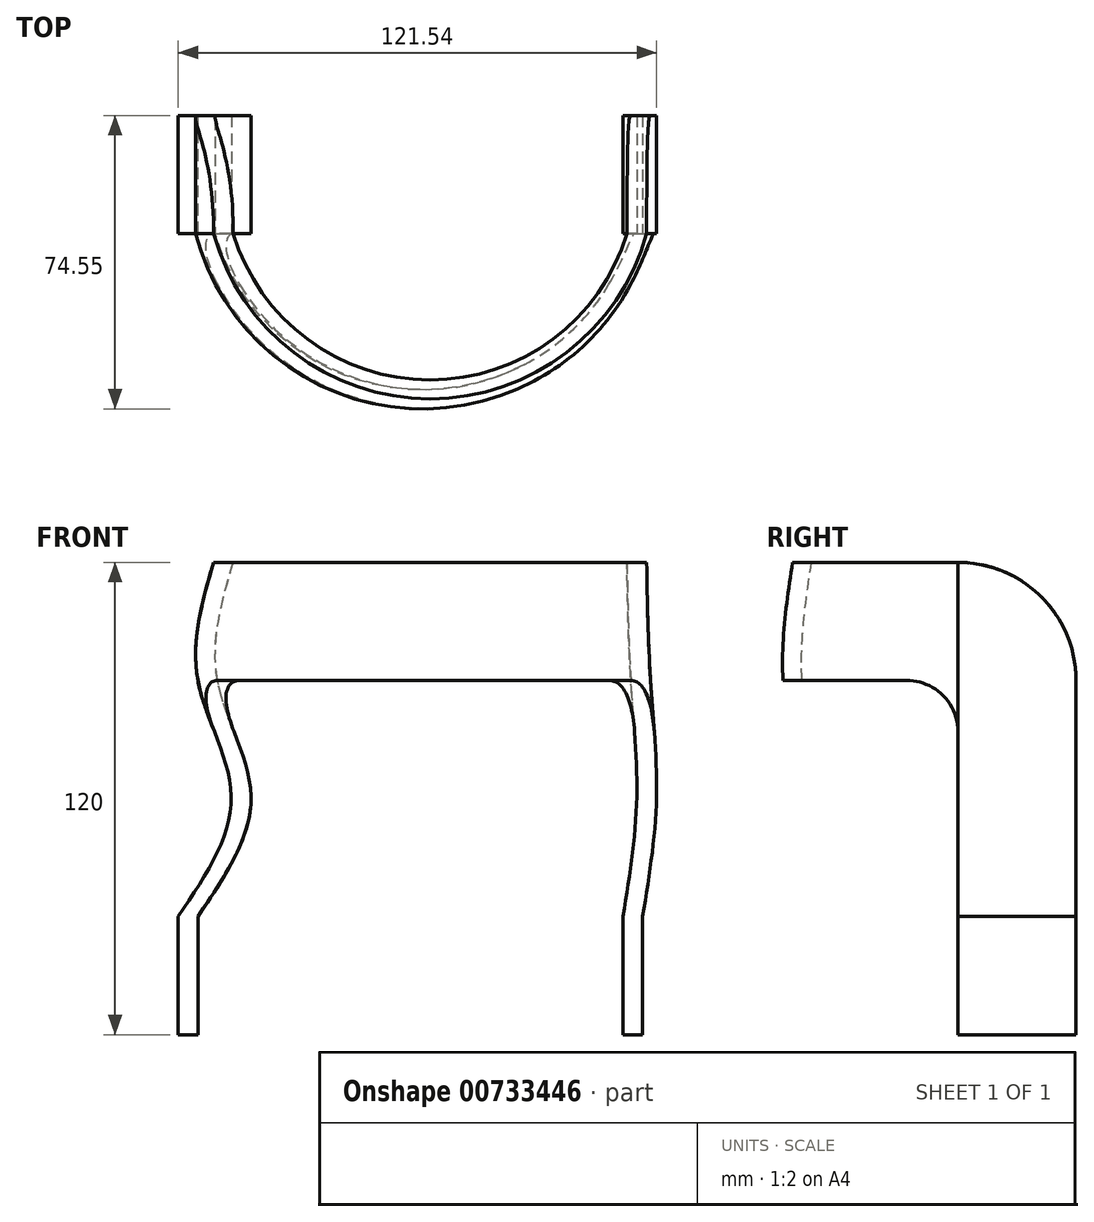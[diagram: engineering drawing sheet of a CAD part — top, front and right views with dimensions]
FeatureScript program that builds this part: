
annotation { "Feature Type Name" : "Feature", "Feature Type Description" : "" }
export const myFeature = defineFeature(function(context is Context, id is Id, definition is map)
    precondition{}
    {
        {
            var Q0;
            Q0=qCreatedBy(makeId("Top.planeOp"),FACE);
            cPlane(context, id + "F0", {"entities" : qUnion([Q0]), "cplaneType" : CPlaneType.OFFSET, "offset" : 30 * mm, "width" : 150 * mm, "height" : 150 * mm});
        }
        {
            var Q0;
            Q0=qCreatedBy(id+"F0.planeOp",FACE);
            var sketch = newSketch(context, id + "F1", { "sketchPlane" : qUnion([Q0])});
            skLineSegment(sketch, "E0", {"start": v(-54, 0) * mm, "end": v(-54, 15) * mm});
            skLineSegment(sketch, "E1", {"start": v(-54, 15) * mm, "end": v(-59, 15) * mm});
            skLineSegment(sketch, "E2", {"start": v(-59, 15) * mm, "end": v(-59, -15) * mm});
            skLineSegment(sketch, "E3", {"start": v(-54, -15) * mm, "end": v(-54, 0) * mm});
            skLineSegment(sketch, "E4", {"start": v(54, 0) * mm, "end": v(54, 15) * mm});
            skLineSegment(sketch, "E5", {"start": v(54, 15) * mm, "end": v(59, 15) * mm});
            skLineSegment(sketch, "E6", {"start": v(59, 15) * mm, "end": v(59, -15) * mm});
            skLineSegment(sketch, "E7", {"start": v(54, -15) * mm, "end": v(54, 0) * mm});
            skArc(sketch, "E8", {"start": v(-54, -15) * mm, "mid": v(0, -56.04) * mm, "end": v(54, -15) * mm});
            skArc(sketch, "E9", {"start": v(59, -15) * mm, "mid": v(0, -60.88) * mm, "end": v(-59, -15) * mm});
            skPoint(sketch, "E10", {"position": v(0, -56.04) * mm});
            skPoint(sketch, "E11", {"position": v(0, -60.88) * mm});
            skSolve(sketch);
        }
        {
            var Q0;
            Q0=qCreatedBy(makeId("Top.planeOp"),FACE);
            var sketch = newSketch(context, id + "F2", { "sketchPlane" : qUnion([Q0])});
            skLineSegment(sketch, "E12", {"start": v(-54, 0) * mm, "end": v(-54, 15) * mm});
            skLineSegment(sketch, "E13", {"start": v(-54, 15) * mm, "end": v(-59, 15) * mm});
            skLineSegment(sketch, "E14", {"start": v(-59, 15) * mm, "end": v(-59, -15) * mm});
            skLineSegment(sketch, "E15", {"start": v(-54, -15) * mm, "end": v(-54, 0) * mm});
            skLineSegment(sketch, "E16", {"start": v(54, 0) * mm, "end": v(54, 15) * mm});
            skLineSegment(sketch, "E17", {"start": v(54, 15) * mm, "end": v(59, 15) * mm});
            skLineSegment(sketch, "E18", {"start": v(59, 15) * mm, "end": v(59, -15) * mm});
            skLineSegment(sketch, "E19", {"start": v(54, -15) * mm, "end": v(54, 0) * mm});
            skArc(sketch, "E20", {"start": v(-54, -15) * mm, "mid": v(0, -56.04) * mm, "end": v(54, -15) * mm});
            skArc(sketch, "E21", {"start": v(59, -15) * mm, "mid": v(0, -60.88) * mm, "end": v(-59, -15) * mm});
            skPoint(sketch, "E22", {"position": v(0, -56.04) * mm});
            skPoint(sketch, "E23", {"position": v(0, -60.88) * mm});
            skSolve(sketch);
        }
        {
            var Q0;
            Q0=qCreatedBy(makeId("Top.planeOp"),FACE);
            cPlane(context, id + "F3", {"entities" : qUnion([Q0]), "cplaneType" : CPlaneType.OFFSET, "offset" : 60 * mm, "width" : 150 * mm, "height" : 150 * mm});
        }
        {
            var Q0;
            Q0=qCreatedBy(id+"F3.planeOp",FACE);
            var sketch = newSketch(context, id + "F4", { "sketchPlane" : qUnion([Q0])});
            skPoint(sketch, "E24", {"position": v(8.5, 0) * mm});
            skPoint(sketch, "E25", {"position": v(-40.5, 0) * mm});
            skPoint(sketch, "E26", {"position": v(57.5, 0) * mm});
            skLineSegment(sketch, "E27", {"start": v(-40.5, 0) * mm, "end": v(-40.5, -15) * mm});
            skLineSegment(sketch, "E28", {"start": v(-45.5, -15) * mm, "end": v(-45.5, 15) * mm});
            skLineSegment(sketch, "E29", {"start": v(-45.5, 15) * mm, "end": v(-40.5, 15) * mm});
            skLineSegment(sketch, "E30", {"start": v(-40.5, 15) * mm, "end": v(-40.5, 0) * mm});
            skLineSegment(sketch, "E31", {"start": v(57.5, 0) * mm, "end": v(57.5, 15) * mm});
            skLineSegment(sketch, "E32", {"start": v(57.5, 15) * mm, "end": v(62.5, 15) * mm});
            skLineSegment(sketch, "E33", {"start": v(62.5, 15) * mm, "end": v(62.5, -15) * mm});
            skLineSegment(sketch, "E34", {"start": v(57.5, -15) * mm, "end": v(57.5, 0) * mm});
            skArc(sketch, "E35", {"start": v(-40.5, -15) * mm, "mid": v(8.5, -51.24) * mm, "end": v(57.5, -15) * mm});
            skArc(sketch, "E36", {"start": v(-45.5, -15) * mm, "mid": v(8.5, -56.04) * mm, "end": v(62.5, -15) * mm});
            skSolve(sketch);
        }
        {
            var Q0;
            Q0=qCreatedBy(makeId("Top.planeOp"),FACE);
            cPlane(context, id + "F5", {"entities" : qUnion([Q0]), "cplaneType" : CPlaneType.OFFSET, "offset" : 90 * mm, "width" : 150 * mm, "height" : 150 * mm});
        }
        {
            var Q0;
            Q0=qCreatedBy(id+"F5.planeOp",FACE);
            var sketch = newSketch(context, id + "F6", { "sketchPlane" : qUnion([Q0])});
            skPoint(sketch, "E37", {"position": v(3.5, 0) * mm});
            skPoint(sketch, "E38", {"position": v(-49, 0) * mm});
            skPoint(sketch, "E39", {"position": v(56, 0) * mm});
            skLineSegment(sketch, "E40", {"start": v(-49, 0) * mm, "end": v(-49, 15) * mm});
            skLineSegment(sketch, "E41", {"start": v(-49, 15) * mm, "end": v(-54, 15) * mm});
            skLineSegment(sketch, "E42", {"start": v(-54, 15) * mm, "end": v(-54, -15) * mm});
            skLineSegment(sketch, "E43", {"start": v(-49, -15) * mm, "end": v(-49, 0) * mm});
            skLineSegment(sketch, "E44", {"start": v(56, 0) * mm, "end": v(56, 15) * mm});
            skLineSegment(sketch, "E45", {"start": v(56, 15) * mm, "end": v(61, 15) * mm});
            skLineSegment(sketch, "E46", {"start": v(61, 15) * mm, "end": v(61, -15) * mm});
            skLineSegment(sketch, "E47", {"start": v(56, -15) * mm, "end": v(56, 0) * mm});
            skArc(sketch, "E48", {"start": v(-49, -15) * mm, "mid": v(3.5, -54.6) * mm, "end": v(56, -15) * mm});
            skArc(sketch, "E49", {"start": v(-54, -15) * mm, "mid": v(3.5, -59.42) * mm, "end": v(61, -15) * mm});
            skSolve(sketch);
        }
        {
            var Q0;
            Q0=qCreatedBy(makeId("Top.planeOp"),FACE);
            cPlane(context, id + "F7", {"entities" : qUnion([Q0]), "cplaneType" : CPlaneType.OFFSET, "offset" : 120 * mm, "width" : 150 * mm, "height" : 150 * mm});
        }
        {
            var Q0;
            Q0=qCreatedBy(id+"F7.planeOp",FACE);
            var sketch = newSketch(context, id + "F8", { "sketchPlane" : qUnion([Q0])});
            skPoint(sketch, "E50", {"position": v(5, 0) * mm});
            skPoint(sketch, "E51", {"position": v(-45, 0) * mm});
            skPoint(sketch, "E52", {"position": v(55, 0) * mm});
            skLineSegment(sketch, "E53", {"start": v(-45, 0) * mm, "end": v(-45, 15) * mm});
            skLineSegment(sketch, "E54", {"start": v(-45, 15) * mm, "end": v(-50, 15) * mm});
            skLineSegment(sketch, "E55", {"start": v(-50, 15) * mm, "end": v(-50, -15) * mm});
            skLineSegment(sketch, "E56", {"start": v(-45, -15) * mm, "end": v(-45, 0) * mm});
            skLineSegment(sketch, "E57", {"start": v(55, 0) * mm, "end": v(55, -15) * mm});
            skLineSegment(sketch, "E58", {"start": v(60, -15) * mm, "end": v(60, 15) * mm});
            skLineSegment(sketch, "E59", {"start": v(60, 15) * mm, "end": v(55, 15) * mm});
            skLineSegment(sketch, "E60", {"start": v(55, 15) * mm, "end": v(55, 0) * mm});
            skArc(sketch, "E61", {"start": v(-45, -15) * mm, "mid": v(5, -52.2) * mm, "end": v(55, -15) * mm});
            skArc(sketch, "E62", {"start": v(-50, -15) * mm, "mid": v(5, -57) * mm, "end": v(60, -15) * mm});
            skSolve(sketch);
        }
        {
            var Q0;
            Q0=makeQuery(id+"F1.imprint","IMPRINT",FACE,{"disambiguationData":[TD([[makeQuery(id+"F1.imprint","IMPRINT",EDGE,{"derivedFrom":sQuery(id+"F1.wireOp",EDGE,"E0")}),1.0]])]});
            var Q1;
            Q1=makeQuery(id+"F4.imprint","IMPRINT",FACE,{"disambiguationData":[TD([[makeQuery(id+"F4.imprint","IMPRINT",EDGE,{"derivedFrom":sQuery(id+"F4.wireOp",EDGE,"E27")}),-1.0]])]});
            var Q2;
            Q2=makeQuery(id+"F6.imprint","IMPRINT",FACE,{"disambiguationData":[TD([[makeQuery(id+"F6.imprint","IMPRINT",EDGE,{"derivedFrom":sQuery(id+"F6.wireOp",EDGE,"E40")}),1.0]])]});
            var Q3;
            Q3=makeQuery(id+"F8.imprint","IMPRINT",FACE,{"disambiguationData":[TD([[makeQuery(id+"F8.imprint","IMPRINT",EDGE,{"derivedFrom":sQuery(id+"F8.wireOp",EDGE,"E53")}),1.0]])]});
            loft(context, id + "F9", {"sheetProfilesArray" : [{ "sheetProfileEntities" : qUnion([Q0]) }, { "sheetProfileEntities" : qUnion([Q1]) }, { "sheetProfileEntities" : qUnion([Q2]) }, { "sheetProfileEntities" : qUnion([Q3]) }]});
        }
        {
            var Q0;
            Q0=makeQuery(id+"F2.imprint","IMPRINT",FACE,{"disambiguationData":[TD([[makeQuery(id+"F2.imprint","IMPRINT",EDGE,{"derivedFrom":sQuery(id+"F2.wireOp",EDGE,"E12")}),1.0]])]});
            extrude(context, id + "F10", {"entities" : qUnion([Q0]), "operationType" : NewBodyOperationType.ADD, "depth" : 30 * mm, "offsetDistance" : 25 * mm});
        }
        {
            var Q0;
            Q0=qCreatedBy(makeId("Right.planeOp"),FACE);
            var sketch = newSketch(context, id + "F11", { "sketchPlane" : qUnion([Q0])});
            skPoint(sketch, "E63", {"position": v(82.65, 59.89) * mm});
            skPoint(sketch, "E64", {"position": v(-15, 120) * mm});
            skPoint(sketch, "E65", {"position": v(-15, 90) * mm});
            skArc(sketch, "E66", {"start": v(-15, 120) * mm, "mid": v(6.21, 111.21) * mm, "end": v(15, 90) * mm});
            skPoint(sketch, "E67", {"position": v(-28.01, 76.99) * mm});
            skArc(sketch, "E68", {"start": v(-15, 76.99) * mm, "mid": v(-18.81, 86.19) * mm, "end": v(-28.01, 90) * mm});
            skLineSegment(sketch, "E69", {"start": v(-15, 76.99) * mm, "end": v(-15, -61.51) * mm});
            skLineSegment(sketch, "E70", {"start": v(-15, -61.51) * mm, "end": v(-141.22, -61.51) * mm});
            skLineSegment(sketch, "E71", {"start": v(-141.22, -61.51) * mm, "end": v(-141.22, 174.74) * mm});
            skLineSegment(sketch, "E72", {"start": v(-141.22, 174.74) * mm, "end": v(85.32, 174.74) * mm});
            skLineSegment(sketch, "E73", {"start": v(85.32, 174.74) * mm, "end": v(15, 90) * mm});
            skLineSegment(sketch, "E74", {"start": v(-28.01, 90) * mm, "end": v(-81.35, 90) * mm});
            skLineSegment(sketch, "E75", {"start": v(-81.35, 90) * mm, "end": v(-81.35, 120) * mm});
            skLineSegment(sketch, "E76", {"start": v(-81.35, 120) * mm, "end": v(-15, 120) * mm});
            skSolve(sketch);
        }
        {
            var Q0;
            Q0 = qSketchRegion(id + "F11", true);
            extrude(context, id + "F12", {"entities" : qUnion([Q0]), "operationType" : NewBodyOperationType.REMOVE, "oppositeDirection" : true, "depth" : 100 * mm, "offsetDistance" : 25 * mm, "hasSecondDirection" : true, "secondDirectionOppositeDirection" : false, "secondDirectionDepth" : 100 * mm});
        }
    });
